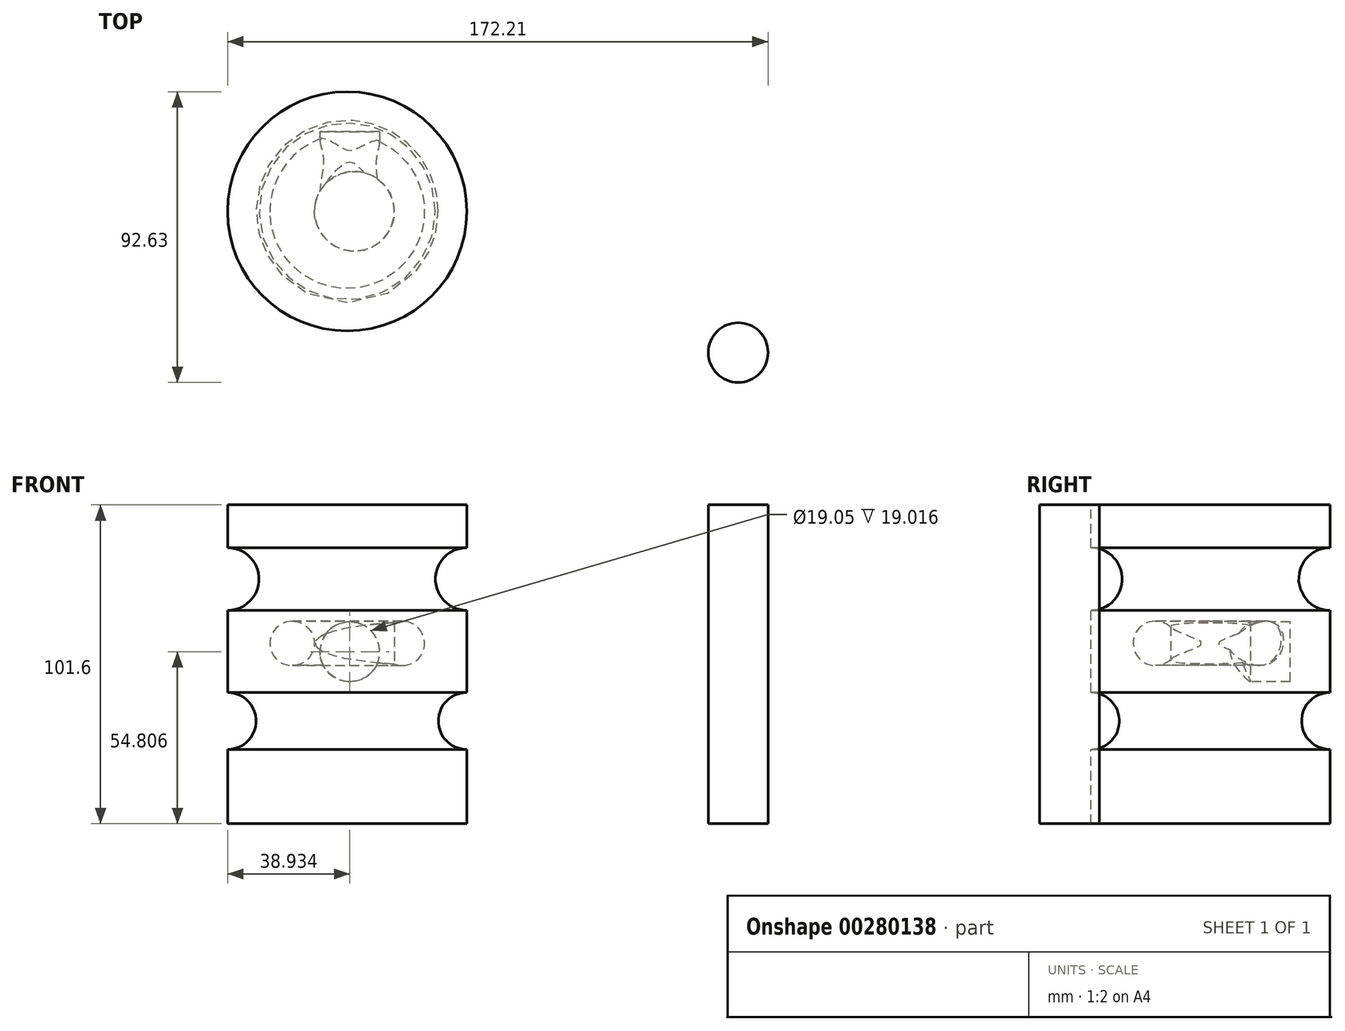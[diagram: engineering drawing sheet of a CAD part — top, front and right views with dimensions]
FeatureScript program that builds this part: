
annotation { "Feature Type Name" : "Feature", "Feature Type Description" : "" }
export const myFeature = defineFeature(function(context is Context, id is Id, definition is map)
    precondition{}
    {
        {
            var Q0;
            Q0=qCreatedBy(makeId("Front.planeOp"),FACE);
            var sketch = newSketch(context, id + "F0", { "sketchPlane" : qUnion([Q0])});
            skLineSegment(sketch, "E0.bottom", {"start": v(-58.81, 101.6) * mm, "end": v(-20.71, 101.6) * mm});
            skLineSegment(sketch, "E0.top", {"start": v(-58.81, 0) * mm, "end": v(-20.71, 0) * mm});
            skLineSegment(sketch, "E0.left", {"start": v(-58.81, 101.6) * mm, "end": v(-58.81, 0) * mm});
            skLineSegment(sketch, "E0.right", {"start": v(-20.71, 101.6) * mm, "end": v(-20.71, 87.96) * mm});
            skArc(sketch, "E1", {"start": v(-20.71, 87.96) * mm, "mid": v(-30.7, 77.97) * mm, "end": v(-20.71, 68) * mm});
            skArc(sketch, "E2", {"start": v(-20.71, 41.82) * mm, "mid": v(-29.78, 32.75) * mm, "end": v(-20.71, 23.68) * mm});
            skLineSegment(sketch, "E3.trimOffspring", {"start": v(-20.71, 68) * mm, "end": v(-20.71, 41.82) * mm});
            skLineSegment(sketch, "E4.trimOffspring", {"start": v(-20.71, 23.68) * mm, "end": v(-20.71, 0) * mm});
            skCircle(sketch, "E5", {"center": v(-41.27, 57.48) * mm, "radius": 7.07 * mm});
            skSolve(sketch);
        }
        {
            var Q0;
            Q0 = qSketchRegion(id + "F0", true);
            var Q1;
            Q1=sQuery(id+"F0.wireOp",EDGE,"E0.left");
            revolve(context, id + "F1", {"entities" : qUnion([Q0]), "axis" : qUnion([Q1]), "revolveType" : RevolveType.FULL});
        }
        {
            var Q0;
            Q0=qCreatedBy(makeId("Front.planeOp"),FACE);
            var sketch = newSketch(context, id + "F2", { "sketchPlane" : qUnion([Q0])});
            skCircle(sketch, "E6", {"center": v(-57.98, 54.8) * mm, "radius": 9.53 * mm});
            skSolve(sketch);
        }
        {
            var Q0;
            Q0 = qSketchRegion(id + "F2", true);
            extrude(context, id + "F3", {"entities" : qUnion([Q0]), "operationType" : NewBodyOperationType.REMOVE, "oppositeDirection" : true, "depth" : 25.4 * mm});
        }
        {
            var Q0;
            Q0=qCreatedBy(makeId("Top.planeOp"),FACE);
            var sketch = newSketch(context, id + "F4", { "sketchPlane" : qUnion([Q0])});
            skCircle(sketch, "E7", {"center": v(-56.53, 0) * mm, "radius": 12.7 * mm});
            skSolve(sketch);
        }
        {
            var Q0;
            Q0 = qSketchRegion(id + "F4", true);
            extrude(context, id + "F5", {"entities" : qUnion([Q0]), "operationType" : NewBodyOperationType.ADD, "depth" : 76.2 * mm});
        }
        {
            var Q0;
            Q0=qCreatedBy(makeId("Top.planeOp"),FACE);
            var sketch = newSketch(context, id + "F6", { "sketchPlane" : qUnion([Q0])});
            skCircle(sketch, "E8", {"center": v(65.78, -45) * mm, "radius": 9.53 * mm});
            skSolve(sketch);
        }
        {
            var Q0;
            Q0 = qSketchRegion(id + "F6", true);
            extrude(context, id + "F7", {"entities" : qUnion([Q0]), "depth" : 101.6 * mm});
        }
    });
